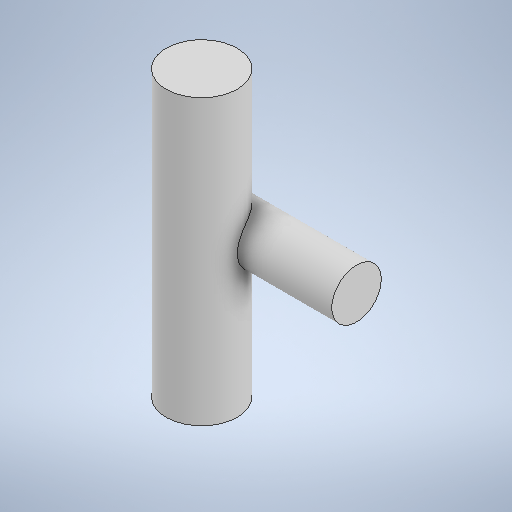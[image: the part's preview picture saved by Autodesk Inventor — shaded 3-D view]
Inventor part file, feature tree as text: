
AUTODESK INVENTOR PART (.ipt)
format: ipt  version: 2025 (Build 290162010, 162A)  size: 247,296 bytes
history: native  units: mm
features: extrude x2, sketch x2
ambient origin geometry x8: Origin, YZ Plane, XZ Plane, XY Plane, X Axis, Y Axis, Z Axis, Center Point
bodies: Solid1 (feature_tree)
feature tree (4):
  extrude  "Extrusion1"  Depth=450.0mm
  extrude  "Extrusion2"  Depth=457.5mm TaperAngle=0.0deg
  sketch  "Sketch1"  dims[d0=250.0mm d1=450.0mm]
  sketch  "Sketch2"  dims[d2=1000.0mm d3=0.0mm d4=457.5mm d5=0.0mm]
